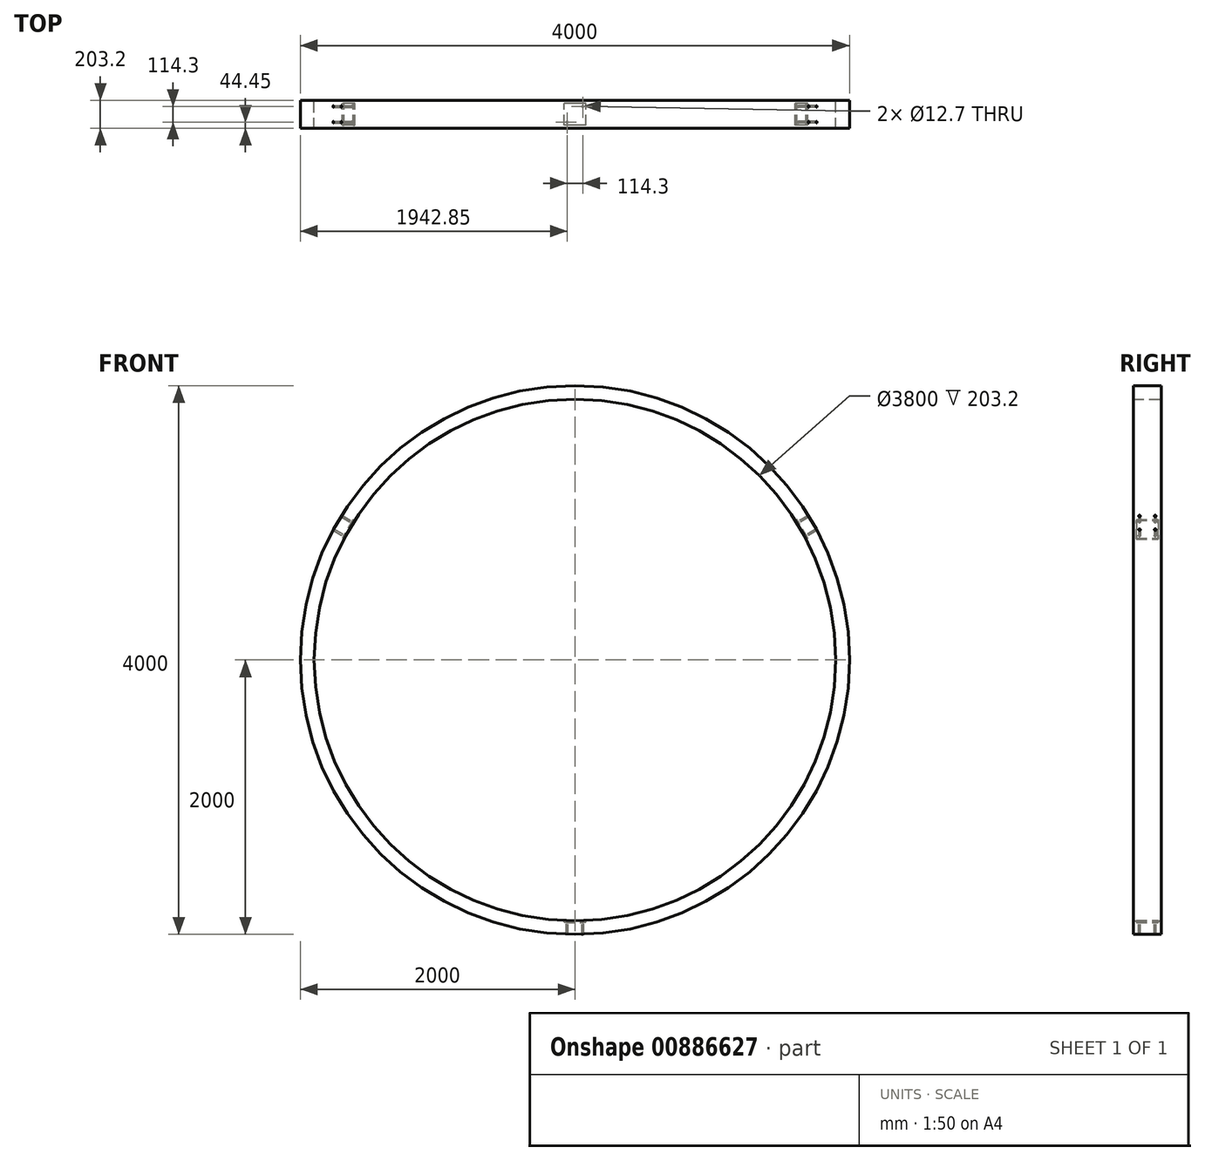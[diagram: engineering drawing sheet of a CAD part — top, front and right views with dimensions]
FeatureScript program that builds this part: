
annotation { "Feature Type Name" : "Feature", "Feature Type Description" : "" }
export const myFeature = defineFeature(function(context is Context, id is Id, definition is map)
    precondition{}
    {
        {
            assignVariable(context, id + "F0", {"name" : "height", "anyValue" : 203.2 * mm});
        }
        {
            var Q0;
            Q0=qCreatedBy(makeId("Front.planeOp"),FACE);
            var sketch = newSketch(context, id + "F1", { "sketchPlane" : qUnion([Q0])});
            skCircle(sketch, "E0", {"center": v(0, 0) * mm, "radius": 1900 * mm});
            skCircle(sketch, "E1", {"center": v(0, 0) * mm, "radius": 2000 * mm});
            skLineSegment(sketch, "E2", {"start": v(0, 0) * mm, "end": v(0, 807.58) * mm, "construction": true});
            skLineSegment(sketch, "E3", {"start": v(0, 1059.46) * mm, "end": v(0, -1141.06) * mm});
            skSolve(sketch);
        }
        {
            var Q0;
            Q0=makeQuery(id+"F1.imprint","IMPRINT",FACE,{"disambiguationData":[TD([[makeQuery(id+"F1.imprint","IMPRINT",EDGE,{"derivedFrom":sQuery(id+"F1.wireOp",EDGE,"E0")}),-1.0]])]});
            extrude(context, id + "F2", {"entities" : qUnion([Q0]), "endBound" : BoundingType.SYMMETRIC, "depth" : getVariable(context, 'height'), "offsetDistance" : 25.4 * mm});
        }
        {
            var Q0;
            Q0=qCreatedBy(makeId("Top.planeOp"),FACE);
            var sketch = newSketch(context, id + "F3", { "sketchPlane" : qUnion([Q0])});
            skLineSegment(sketch, "E4", {"start": v(0, 83.45) * mm, "end": v(0, -223.81) * mm});
            skSolve(sketch);
        }
        {
            var Q0;
            Q0=qCreatedBy(makeId("Top.planeOp"),FACE);
            var Q1;
            Q1=sQuery(id+"F3.wireOp",EDGE,"E4");
            cPlane(context, id + "F4", {"entities" : qUnion([Q0, Q1]), "cplaneType" : CPlaneType.LINE_ANGLE, "offset" : 25.4 * mm, "angle" : 120 * degree, "width" : 152.4 * mm, "height" : 152.4 * mm});
        }
        {
            var Q0;
            Q0=qCreatedBy(makeId("Top.planeOp"),FACE);
            var Q1;
            Q1=sQuery(id+"F3.wireOp",EDGE,"E4");
            cPlane(context, id + "F5", {"entities" : qUnion([Q0, Q1]), "cplaneType" : CPlaneType.LINE_ANGLE, "offset" : 25.4 * mm, "angle" : 240 * degree, "width" : 152.4 * mm, "height" : 152.4 * mm});
        }
        {
            var Q0;
            Q0=qCreatedBy(makeId("Top.planeOp"),FACE);
            var sketch = newSketch(context, id + "F6", { "sketchPlane" : qUnion([Q0])});
            skLineSegment(sketch, "E5.bottom", {"start": v(79.38, -79.38) * mm, "end": v(-79.38, -79.38) * mm});
            skLineSegment(sketch, "E5.top", {"start": v(79.38, 79.38) * mm, "end": v(-79.38, 79.37) * mm});
            skLineSegment(sketch, "E5.left", {"start": v(79.38, -79.38) * mm, "end": v(79.38, 79.38) * mm});
            skLineSegment(sketch, "E5.right", {"start": v(-79.38, -79.38) * mm, "end": v(-79.38, 79.38) * mm});
            skPoint(sketch, "E5.middle", {"position": v(0, 0) * mm});
            skSolve(sketch);
        }
        {
            var Q0;
            Q0=makeQuery(id+"F6.imprint","IMPRINT",FACE,{"disambiguationData":[TD([[makeQuery(id+"F6.imprint","IMPRINT",EDGE,{"derivedFrom":sQuery(id+"F6.wireOp",EDGE,"E5.bottom")}),-1.0]])]});
            var Q1;
            Q1=makeQuery(id+"F2.opExtrude","SWEPT_FACE",FACE,{"disambiguationData":[OSD([sQuery(id+"F1.wireOp",EDGE,"E0")])]});
            extrude(context, id + "F7", {"entities" : qUnion([Q0]), "operationType" : NewBodyOperationType.REMOVE, "endBound" : BoundingType.UP_TO_SURFACE, "oppositeDirection" : true, "depth" : 609.6 * mm, "endBoundEntityFace" : qUnion([Q1]), "hasOffset" : true, "offsetDistance" : 12.7 * mm, "offsetOppositeDirection" : true});
        }
        {
            var Q0;
            Q0=qCreatedBy(id+"F4.planeOp",FACE);
            var sketch = newSketch(context, id + "F8", { "sketchPlane" : qUnion([Q0])});
            skLineSegment(sketch, "E6.bottom", {"start": v(-79.37, -79.37) * mm, "end": v(79.38, -79.37) * mm});
            skLineSegment(sketch, "E6.top", {"start": v(-79.38, 79.38) * mm, "end": v(79.37, 79.38) * mm});
            skLineSegment(sketch, "E6.left", {"start": v(-79.37, -79.37) * mm, "end": v(-79.38, 79.38) * mm});
            skLineSegment(sketch, "E6.right", {"start": v(79.38, -79.37) * mm, "end": v(79.37, 79.38) * mm});
            skPoint(sketch, "E6.middle", {"position": v(0, 0) * mm});
            skSolve(sketch);
        }
        {
            var Q0;
            Q0 = qSketchRegion(id + "F8", true);
            var Q1;
            Q1=makeQuery(id+"F2.opExtrude","SWEPT_FACE",FACE,{"disambiguationData":[OSD([sQuery(id+"F1.wireOp",EDGE,"E0")])]});
            extrude(context, id + "F9", {"entities" : qUnion([Q0]), "operationType" : NewBodyOperationType.REMOVE, "endBound" : BoundingType.UP_TO_SURFACE, "depth" : 609.6 * mm, "endBoundEntityFace" : qUnion([Q1]), "hasOffset" : true, "offsetDistance" : 12.7 * mm, "offsetOppositeDirection" : true});
        }
        {
            var Q0;
            Q0=qCreatedBy(id+"F5.planeOp",FACE);
            var sketch = newSketch(context, id + "F10", { "sketchPlane" : qUnion([Q0])});
            skLineSegment(sketch, "E7.bottom", {"start": v(79.38, 79.37) * mm, "end": v(-79.37, 79.37) * mm});
            skLineSegment(sketch, "E7.top", {"start": v(79.37, -79.38) * mm, "end": v(-79.38, -79.38) * mm});
            skLineSegment(sketch, "E7.left", {"start": v(79.38, 79.37) * mm, "end": v(79.37, -79.38) * mm});
            skLineSegment(sketch, "E7.right", {"start": v(-79.37, 79.37) * mm, "end": v(-79.38, -79.38) * mm});
            skPoint(sketch, "E7.middle", {"position": v(0, 0) * mm});
            skSolve(sketch);
        }
        {
            var Q0;
            Q0 = qSketchRegion(id + "F10", true);
            var Q1;
            Q1=makeQuery(id+"F2.opExtrude","SWEPT_FACE",FACE,{"disambiguationData":[OSD([sQuery(id+"F1.wireOp",EDGE,"E0")])]});
            extrude(context, id + "F11", {"entities" : qUnion([Q0]), "operationType" : NewBodyOperationType.REMOVE, "endBound" : BoundingType.UP_TO_SURFACE, "depth" : 609.6 * mm, "endBoundEntityFace" : qUnion([Q1]), "hasOffset" : true, "offsetDistance" : 12.7 * mm, "offsetOppositeDirection" : true});
        }
        {
            var Q0;
            Q0=qCreatedBy(id+"F4.planeOp",FACE);
            var sketch = newSketch(context, id + "F12", { "sketchPlane" : qUnion([Q0])});
            skCircle(sketch, "E8", {"center": v(57.15, -57.15) * mm, "radius": 6.35 * mm});
            skCircle(sketch, "E9.MirrorC", {"center": v(57.15, 57.15) * mm, "radius": 6.35 * mm});
            skLineSegment(sketch, "E10", {"start": v(0, -157.36) * mm, "end": v(0, 90.5) * mm, "construction": true});
            skCircle(sketch, "E11.MirrorC", {"center": v(-57.15, -57.15) * mm, "radius": 6.35 * mm});
            skCircle(sketch, "E12.MirrorC", {"center": v(-57.15, 57.15) * mm, "radius": 6.35 * mm});
            skSolve(sketch);
        }
        {
            var Q0;
            Q0 = qSketchRegion(id + "F12", true);
            extrude(context, id + "F13", {"entities" : qUnion([Q0]), "operationType" : NewBodyOperationType.REMOVE, "endBound" : BoundingType.THROUGH_ALL, "depth" : 762 * mm, "offsetDistance" : 25.4 * mm});
        }
        {
            var Q0;
            Q0=qCreatedBy(id+"F5.planeOp",FACE);
            var sketch = newSketch(context, id + "F14", { "sketchPlane" : qUnion([Q0])});
            skCircle(sketch, "E13", {"center": v(-57.15, 57.15) * mm, "radius": 6.35 * mm});
            skLineSegment(sketch, "E14", {"start": v(0, 114.48) * mm, "end": v(0, -27.7) * mm, "construction": true});
            skCircle(sketch, "E15.MirrorC", {"center": v(-57.15, -57.15) * mm, "radius": 6.35 * mm});
            skCircle(sketch, "E16.MirrorC", {"center": v(57.15, 57.15) * mm, "radius": 6.35 * mm});
            skCircle(sketch, "E17.MirrorC", {"center": v(57.15, -57.15) * mm, "radius": 6.35 * mm});
            skSolve(sketch);
        }
        {
            var Q0;
            Q0 = qSketchRegion(id + "F14", true);
            extrude(context, id + "F15", {"entities" : qUnion([Q0]), "operationType" : NewBodyOperationType.REMOVE, "endBound" : BoundingType.THROUGH_ALL, "depth" : 762 * mm, "offsetDistance" : 25.4 * mm});
        }
        {
            var Q0;
            Q0=qCreatedBy(makeId("Top.planeOp"),FACE);
            var sketch = newSketch(context, id + "F16", { "sketchPlane" : qUnion([Q0])});
            skCircle(sketch, "E18", {"center": v(57.15, 57.15) * mm, "radius": 6.35 * mm});
            skLineSegment(sketch, "E19", {"start": v(124.66, 0) * mm, "end": v(-46.34, 0) * mm, "construction": true});
            skCircle(sketch, "E20.MirrorC", {"center": v(-57.15, 57.15) * mm, "radius": 6.35 * mm});
            skCircle(sketch, "E21.MirrorC", {"center": v(-57.15, -57.15) * mm, "radius": 6.35 * mm});
            skCircle(sketch, "E22.MirrorC", {"center": v(57.15, -57.15) * mm, "radius": 6.35 * mm});
            skSolve(sketch);
        }
        {
            var Q0;
            Q0=makeQuery(id+"F16.imprint","IMPRINT",FACE,{"disambiguationData":[TD([[makeQuery(id+"F16.imprint","IMPRINT",EDGE,{"derivedFrom":sQuery(id+"F16.wireOp",EDGE,"E18")}),1.0]])]});
            var Q1;
            Q1=makeQuery(id+"F16.imprint","IMPRINT",FACE,{"disambiguationData":[TD([[makeQuery(id+"F16.imprint","IMPRINT",EDGE,{"derivedFrom":sQuery(id+"F16.wireOp",EDGE,"E22.MirrorC")}),-1.0]])]});
            var Q2;
            Q2=makeQuery(id+"F16.imprint","IMPRINT",FACE,{"disambiguationData":[TD([[makeQuery(id+"F16.imprint","IMPRINT",EDGE,{"derivedFrom":sQuery(id+"F16.wireOp",EDGE,"E21.MirrorC")}),1.0]])]});
            var Q3;
            Q3=makeQuery(id+"F16.imprint","IMPRINT",FACE,{"disambiguationData":[TD([[makeQuery(id+"F16.imprint","IMPRINT",EDGE,{"derivedFrom":sQuery(id+"F16.wireOp",EDGE,"E20.MirrorC")}),-1.0]])]});
            extrude(context, id + "F17", {"entities" : qUnion([Q0, Q1, Q2, Q3]), "operationType" : NewBodyOperationType.REMOVE, "endBound" : BoundingType.THROUGH_ALL, "oppositeDirection" : true, "depth" : 762 * mm, "offsetDistance" : 25.4 * mm});
        }
    });
